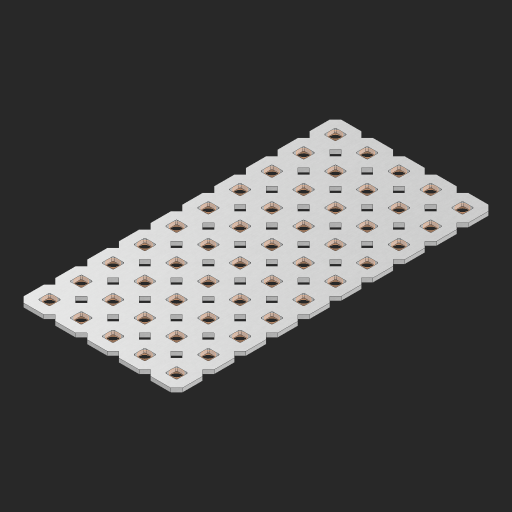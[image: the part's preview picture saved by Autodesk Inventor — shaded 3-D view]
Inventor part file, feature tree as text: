
AUTODESK INVENTOR PART (.ipt)
format: ipt  version: 2023 (Build 270158000, 158)  size: 878,080 bytes
history: native  units: in
note: dims shown in document units (in); Inventor stores cm internally (conversion verified against a paired STEP export)
features: other x51, extrude x49, sketch x2, pattern_linear x1
ambient origin geometry x8: Origin, YZ Plane, XZ Plane, XY Plane, X Axis, Y Axis, Z Axis, Center Point
bodies: Solid1 (feature_tree), Body (feature_tree)
feature tree (103):
  pattern_linear  "Rectangular Pattern1"  Spacing1=0.09in  [1 undecoded]
  sketch  "Sketch1"  dims[d1=0.5in]
  sketch  "Sketch2"  dims[d2=0.182in d3=0.09in d4=0.09in d5=0.09in d6=0.09in d7=0.09in d8=0.09in d9=0.09in d10=0.09in d11=0.02in d13=0.0in d14=0.172in d15=0.0625in d16=0.0in d19=0.5in d22=0.5in]
  other  "Srf1"
  other  "Srf126"
  other  "Srf127"
  other  "Srf128"
  other  "Srf129"
  other  "Srf130"
  other  "Srf131"
  other  "Srf250"
  other  "Srf251"
  other  "Srf252"
  other  "Srf268"
  other  "Srf269"
  other  "Srf270"
  other  "Srf271"
  other  "Srf272"
  other  "Srf273"
  other  "Srf274"
  other  "Srf275"
  other  "Srf276"
  other  "Srf277"
  other  "Srf293"
  other  "Srf294"
  other  "Srf295"
  other  "Srf296"
  other  "Srf297"
  other  "Srf298"
  other  "Srf299"
  other  "Srf300"
  other  "Srf301"
  other  "Srf302"
  other  "Srf318"
  other  "Srf319"
  other  "Srf320"
  other  "Srf321"
  other  "Srf322"
  other  "Srf323"
  other  "Srf324"
  other  "Srf325"
  other  "Srf326"
  other  "Srf327"
  other  "Srf343"
  other  "Srf344"
  other  "Srf345"
  other  "Srf346"
  other  "Srf347"
  other  "Srf348"
  other  "Srf349"
  other  "Srf350"
  other  "Srf351"
  other  "Srf352"
  other  "Circle"
  extrude  "ExtrusionSrf126"  Depth=0.09in
  extrude  "ExtrusionSrf127"  Depth=0.09in
  extrude  "ExtrusionSrf128"  Depth=0.09in
  extrude  "ExtrusionSrf129"  Depth=0.09in
  extrude  "ExtrusionSrf130"  Depth=0.09in
  extrude  "ExtrusionSrf131"  Depth=0.09in
  extrude  "ExtrusionSrf250"  Depth=0.09in
  extrude  "ExtrusionSrf251"  Depth=0.02in
  extrude  "ExtrusionSrf252"  TaperAngle=0.0deg  [1 undecoded]
  extrude  "ExtrusionSrf268"  Depth=0.5in
  extrude  "ExtrusionSrf269"  Depth=0.0625in TaperAngle=0.0deg
  extrude  "ExtrusionSrf270"  Depth=0.5in
  extrude  "ExtrusionSrf271"  Depth=0.5in
  extrude  "ExtrusionSrf272"  [1 undecoded]
  extrude  "ExtrusionSrf273"  [1 undecoded]
  extrude  "ExtrusionSrf274"  [1 undecoded]
  extrude  "ExtrusionSrf275"  [1 undecoded]
  extrude  "ExtrusionSrf276"  [1 undecoded]
  extrude  "ExtrusionSrf277"  [1 undecoded]
  extrude  "ExtrusionSrf293"  [1 undecoded]
  extrude  "ExtrusionSrf294"  [1 undecoded]
  extrude  "ExtrusionSrf295"  [1 undecoded]
  extrude  "ExtrusionSrf296"  [1 undecoded]
  extrude  "ExtrusionSrf297"  [1 undecoded]
  extrude  "ExtrusionSrf298"  [1 undecoded]
  extrude  "ExtrusionSrf299"  [1 undecoded]
  extrude  "ExtrusionSrf300"  [1 undecoded]
  extrude  "ExtrusionSrf301"  [1 undecoded]
  extrude  "ExtrusionSrf302"  [1 undecoded]
  extrude  "ExtrusionSrf318"  [1 undecoded]
  extrude  "ExtrusionSrf319"  [1 undecoded]
  extrude  "ExtrusionSrf320"  [1 undecoded]
  extrude  "ExtrusionSrf321"  [1 undecoded]
  extrude  "ExtrusionSrf322"  [1 undecoded]
  extrude  "ExtrusionSrf323"  [1 undecoded]
  extrude  "ExtrusionSrf324"  [1 undecoded]
  extrude  "ExtrusionSrf325"  [1 undecoded]
  extrude  "ExtrusionSrf326"  [1 undecoded]
  extrude  "ExtrusionSrf327"  [1 undecoded]
  extrude  "ExtrusionSrf343"  [1 undecoded]
  extrude  "ExtrusionSrf344"  [1 undecoded]
  extrude  "ExtrusionSrf345"  [1 undecoded]
  extrude  "ExtrusionSrf346"  [1 undecoded]
  extrude  "ExtrusionSrf347"  [1 undecoded]
  extrude  "ExtrusionSrf348"  [1 undecoded]
  extrude  "ExtrusionSrf349"  [1 undecoded]
  extrude  "ExtrusionSrf350"  [1 undecoded]
  extrude  "ExtrusionSrf351"  [1 undecoded]
  extrude  "ExtrusionSrf352"  [1 undecoded]
note: 38 required parameter values undecoded (feature->parameter linkage not recoverable at this tier; creation-order binding heuristic only, values carry confidence <= 0.55)
